annotation { "Feature Type Name" : "Feature", "Feature Type Description" : "" }
export const myFeature = defineFeature(function(context is Context, id is Id, definition is map)
    precondition{}
    {
        {
            var Q0;
            Q0=qCreatedBy(makeId("Top.planeOp"),FACE);
            var sketch = newSketch(context, id + "F0", { "sketchPlane" : qUnion([Q0])});
            skLineSegment(sketch, "E0.bottom", {"start": v(88.9, 50.8) * mm, "end": v(-88.9, 50.8) * mm});
            skLineSegment(sketch, "E0.top", {"start": v(88.9, -50.8) * mm, "end": v(-88.9, -50.8) * mm});
            skLineSegment(sketch, "E0.left", {"start": v(88.9, 50.8) * mm, "end": v(88.9, -50.8) * mm});
            skLineSegment(sketch, "E0.right", {"start": v(-88.9, 50.8) * mm, "end": v(-88.9, -50.8) * mm});
            skPoint(sketch, "E0.middle", {"position": v(0, 0) * mm});
            skText(sketch, "E1", { "text": "Brandon Ortega", "fontName": "OpenSans-Regular.ttf"});
            skLineSegment(sketch, "E2.bottom", {"start": v(95.25, 57.15) * mm, "end": v(-95.25, 57.15) * mm});
            skLineSegment(sketch, "E2.top", {"start": v(95.25, -57.15) * mm, "end": v(-95.25, -57.15) * mm});
            skLineSegment(sketch, "E2.left", {"start": v(95.25, 57.15) * mm, "end": v(95.25, -57.15) * mm});
            skLineSegment(sketch, "E2.right", {"start": v(-95.25, 57.15) * mm, "end": v(-95.25, -57.15) * mm});
            skLineSegment(sketch, "E3", {"start": v(-82.55, -15.2) * mm, "end": v(58.84, -15.2) * mm});
            skLineSegment(sketch, "E4", {"start": v(-82.55, -15.2) * mm, "end": v(-74.57, -13.6) * mm});
            skLineSegment(sketch, "E5", {"start": v(-74.57, -13.6) * mm, "end": v(-74.57, -11.23) * mm});
            skLineSegment(sketch, "E6", {"start": v(-74.57, -11.23) * mm, "end": v(-44.1, -11.23) * mm});
            skLineSegment(sketch, "E7", {"start": v(-44.1, -11.23) * mm, "end": v(-44.1, -10.52) * mm});
            skLineSegment(sketch, "E8", {"start": v(-44.1, -10.52) * mm, "end": v(-39.37, -8.24) * mm});
            skLineSegment(sketch, "E9", {"start": v(-39.37, -8.24) * mm, "end": v(-35.5, -8.24) * mm});
            skLineSegment(sketch, "E10", {"start": v(-35.5, -8.24) * mm, "end": v(-35.5, -5.61) * mm});
            skLineSegment(sketch, "E11", {"start": v(-35.5, -5.61) * mm, "end": v(-32.66, -5.61) * mm});
            skLineSegment(sketch, "E12", {"start": v(-32.66, -5.61) * mm, "end": v(-21.7, -9) * mm});
            skFitSpline(sketch, "E13", {"points": [v(-21.7, -9) * mm, v(-19.63, -9.48) * mm, v(-17.36, -9.15) * mm], "startDerivative": vector(4.23, -1.18) * mm, "endDerivative": vector(5.03, -0.02) * mm});
            skLineSegment(sketch, "E14", {"start": v(-17.36, -9.15) * mm, "end": v(11.51, -9.15) * mm});
            skLineSegment(sketch, "E15", {"start": v(11.51, -9.15) * mm, "end": v(12.43, -9.9) * mm});
            skLineSegment(sketch, "E16", {"start": v(12.43, -9.9) * mm, "end": v(12.43, -10.89) * mm});
            skLineSegment(sketch, "E17", {"start": v(12.43, -10.89) * mm, "end": v(53.63, -10.89) * mm});
            skLineSegment(sketch, "E18", {"start": v(53.63, -10.89) * mm, "end": v(54.2, -11.57) * mm});
            skLineSegment(sketch, "E19", {"start": v(54.2, -11.57) * mm, "end": v(54.2, -13.42) * mm});
            skLineSegment(sketch, "E20", {"start": v(54.2, -13.42) * mm, "end": v(58.84, -13.42) * mm});
            skLineSegment(sketch, "E21", {"start": v(58.84, -13.42) * mm, "end": v(58.84, -15.2) * mm});
            skLineSegment(sketch, "E22.MirrorCS", {"start": v(58.84, -17) * mm, "end": v(58.84, -15.2) * mm});
            skLineSegment(sketch, "E23.MirrorCS", {"start": v(54.2, -17) * mm, "end": v(58.84, -17) * mm});
            skLineSegment(sketch, "E24.MirrorCS", {"start": v(54.2, -18.85) * mm, "end": v(54.2, -17) * mm});
            skLineSegment(sketch, "E25.MirrorCS", {"start": v(53.63, -19.53) * mm, "end": v(54.2, -18.85) * mm});
            skLineSegment(sketch, "E26.MirrorCS", {"start": v(12.43, -19.53) * mm, "end": v(53.63, -19.53) * mm});
            skLineSegment(sketch, "E27.MirrorCS", {"start": v(12.43, -20.52) * mm, "end": v(12.43, -19.53) * mm});
            skLineSegment(sketch, "E28.MirrorCS", {"start": v(11.51, -21.27) * mm, "end": v(12.43, -20.52) * mm});
            skLineSegment(sketch, "E29.MirrorCS", {"start": v(-17.36, -21.27) * mm, "end": v(11.51, -21.27) * mm});
            skFitSpline(sketch, "E30.MirrorCS", {"points": [v(-21.7, -21.41) * mm, v(-19.63, -20.94) * mm, v(-17.36, -21.27) * mm], "startDerivative": vector(4.23, 1.18) * mm, "endDerivative": vector(5.03, 0.02) * mm});
            skLineSegment(sketch, "E31.MirrorCS", {"start": v(-32.66, -24.8) * mm, "end": v(-21.7, -21.41) * mm});
            skLineSegment(sketch, "E32.MirrorCS", {"start": v(-35.5, -24.8) * mm, "end": v(-32.66, -24.8) * mm});
            skLineSegment(sketch, "E33.MirrorCS", {"start": v(-35.5, -22.18) * mm, "end": v(-35.5, -24.8) * mm});
            skLineSegment(sketch, "E34.MirrorCS", {"start": v(-39.37, -22.18) * mm, "end": v(-35.5, -22.18) * mm});
            skLineSegment(sketch, "E35.MirrorCS", {"start": v(-44.1, -19.9) * mm, "end": v(-39.37, -22.18) * mm});
            skLineSegment(sketch, "E36.MirrorCS", {"start": v(-44.1, -19.2) * mm, "end": v(-44.1, -19.9) * mm});
            skLineSegment(sketch, "E37.MirrorCS", {"start": v(-74.57, -19.2) * mm, "end": v(-44.1, -19.2) * mm});
            skLineSegment(sketch, "E38.MirrorCS", {"start": v(-74.57, -16.82) * mm, "end": v(-74.57, -19.2) * mm});
            skLineSegment(sketch, "E39.MirrorCS", {"start": v(-82.55, -15.2) * mm, "end": v(-74.57, -16.82) * mm});
            skLineSegment(sketch, "E40", {"start": v(58.84, -13.42) * mm, "end": v(61.69, -13.42) * mm});
            skLineSegment(sketch, "E41", {"start": v(58.84, -17) * mm, "end": v(61.69, -17) * mm});
            skLineSegment(sketch, "E42", {"start": v(61.69, -13.42) * mm, "end": v(61.69, -17) * mm});
            skLineSegment(sketch, "E43", {"start": v(58.84, -15.2) * mm, "end": v(61.69, -15.2) * mm});
            skLineSegment(sketch, "E44", {"start": v(-19.8, -9.15) * mm, "end": v(-19.8, -4.07) * mm});
            skLineSegment(sketch, "E45", {"start": v(-19.8, -4.07) * mm, "end": v(-26.99, 3.12) * mm});
            skLineSegment(sketch, "E46", {"start": v(-16.63, -9.15) * mm, "end": v(-16.63, -3.81) * mm});
            skLineSegment(sketch, "E47", {"start": v(-14.09, -9.15) * mm, "end": v(-14.09, -3.3) * mm});
            skLineSegment(sketch, "E48", {"start": v(-14.09, -3.3) * mm, "end": v(-23.07, 5.68) * mm});
            skLineSegment(sketch, "E49", {"start": v(-10.91, -9.15) * mm, "end": v(-10.91, -3.05) * mm});
            skLineSegment(sketch, "E50", {"start": v(-8.37, -9.15) * mm, "end": v(-8.37, -2.8) * mm});
            skLineSegment(sketch, "E51", {"start": v(-8.37, -2.8) * mm, "end": v(-19.15, 7.98) * mm});
            skLineSegment(sketch, "E52", {"start": v(-5.2, -9.15) * mm, "end": v(-5.2, -2.54) * mm});
            skLineSegment(sketch, "E53", {"start": v(-24.73, 5.35) * mm, "end": v(-16.63, -3.81) * mm});
            skLineSegment(sketch, "E54", {"start": v(-20.82, 7.92) * mm, "end": v(-10.91, -3.05) * mm});
            skLineSegment(sketch, "E55", {"start": v(-16.9, 10.22) * mm, "end": v(-5.2, -2.54) * mm});
            skLineSegment(sketch, "E56.MirrorCS", {"start": v(-1.17, -21.27) * mm, "end": v(-1.17, -27.88) * mm});
            skLineSegment(sketch, "E57.MirrorCS", {"start": v(-0.4, -21.27) * mm, "end": v(-0.4, -27.62) * mm});
            skLineSegment(sketch, "E58.MirrorCS", {"start": v(0.86, -21.27) * mm, "end": v(0.86, -27.37) * mm});
            skLineSegment(sketch, "E59.MirrorCS", {"start": v(1.63, -21.27) * mm, "end": v(1.63, -27.12) * mm});
            skLineSegment(sketch, "E60.MirrorCS", {"start": v(2.9, -21.27) * mm, "end": v(2.9, -26.6) * mm});
            skLineSegment(sketch, "E61.MirrorCS", {"start": v(3.66, -21.27) * mm, "end": v(3.66, -26.35) * mm});
            skLineSegment(sketch, "E62.MirrorCS", {"start": v(3.66, -26.35) * mm, "end": v(10.84, -33.54) * mm});
            skLineSegment(sketch, "E63.MirrorCS", {"start": v(10.3, -34.08) * mm, "end": v(2.9, -26.6) * mm});
            skLineSegment(sketch, "E64.MirrorCS", {"start": v(1.63, -27.12) * mm, "end": v(10.6, -36.1) * mm});
            skLineSegment(sketch, "E65.MirrorCS", {"start": v(10.07, -36.64) * mm, "end": v(0.86, -27.37) * mm});
            skLineSegment(sketch, "E66.MirrorCS", {"start": v(-0.4, -27.62) * mm, "end": v(10.37, -38.4) * mm});
            skLineSegment(sketch, "E67.MirrorCS", {"start": v(9.83, -38.94) * mm, "end": v(-1.17, -27.88) * mm});
            skLineSegment(sketch, "E68.MirrorCS", {"start": v(2.9, -9.15) * mm, "end": v(2.9, -2.54) * mm});
            skLineSegment(sketch, "E69.MirrorCS", {"start": v(3.67, -9.15) * mm, "end": v(3.67, -2.8) * mm});
            skLineSegment(sketch, "E70.MirrorCS", {"start": v(4.94, -9.15) * mm, "end": v(4.94, -3.05) * mm});
            skLineSegment(sketch, "E71.MirrorCS", {"start": v(5.7, -9.15) * mm, "end": v(5.7, -3.3) * mm});
            skLineSegment(sketch, "E72.MirrorCS", {"start": v(6.97, -9.15) * mm, "end": v(6.97, -3.81) * mm});
            skLineSegment(sketch, "E73.MirrorCS", {"start": v(7.73, -9.15) * mm, "end": v(7.73, -4.07) * mm});
            skLineSegment(sketch, "E74.MirrorCS", {"start": v(7.73, -4.07) * mm, "end": v(14.92, 3.12) * mm});
            skLineSegment(sketch, "E75.MirrorCS", {"start": v(14.38, 3.66) * mm, "end": v(6.97, -3.81) * mm});
            skLineSegment(sketch, "E76.MirrorCS", {"start": v(5.7, -3.3) * mm, "end": v(14.68, 5.68) * mm});
            skLineSegment(sketch, "E77.MirrorCS", {"start": v(14.14, 6.22) * mm, "end": v(4.94, -3.05) * mm});
            skLineSegment(sketch, "E78.MirrorCS", {"start": v(3.67, -2.8) * mm, "end": v(14.44, 7.98) * mm});
            skLineSegment(sketch, "E79.MirrorCS", {"start": v(13.9, 8.52) * mm, "end": v(2.9, -2.54) * mm});
            skLineSegment(sketch, "E80.MirrorCS", {"start": v(-62.37, -19.2) * mm, "end": v(-62.37, -25.8) * mm});
            skLineSegment(sketch, "E81.MirrorCS", {"start": v(-63.13, -19.2) * mm, "end": v(-63.13, -25.54) * mm});
            skLineSegment(sketch, "E82.MirrorCS", {"start": v(-64.4, -19.2) * mm, "end": v(-64.4, -25.29) * mm});
            skLineSegment(sketch, "E83.MirrorCS", {"start": v(-65.16, -19.2) * mm, "end": v(-65.16, -25.04) * mm});
            skLineSegment(sketch, "E84.MirrorCS", {"start": v(-66.43, -19.2) * mm, "end": v(-66.43, -24.53) * mm});
            skLineSegment(sketch, "E85.MirrorCS", {"start": v(-67.2, -19.2) * mm, "end": v(-67.2, -24.27) * mm});
            skLineSegment(sketch, "E86.MirrorCS", {"start": v(-67.2, -24.27) * mm, "end": v(-74.38, -31.46) * mm});
            skLineSegment(sketch, "E87.MirrorCS", {"start": v(-73.84, -32) * mm, "end": v(-66.43, -24.53) * mm});
            skLineSegment(sketch, "E88.MirrorCS", {"start": v(-65.16, -25.04) * mm, "end": v(-74.14, -34.02) * mm});
            skLineSegment(sketch, "E89.MirrorCS", {"start": v(-73.6, -34.55) * mm, "end": v(-64.4, -25.29) * mm});
            skLineSegment(sketch, "E90.MirrorCS", {"start": v(-63.13, -25.54) * mm, "end": v(-73.9, -36.32) * mm});
            skLineSegment(sketch, "E91.MirrorCS", {"start": v(-73.36, -36.86) * mm, "end": v(-62.37, -25.8) * mm});
            skLineSegment(sketch, "E92", {"start": v(13.9, 8.52) * mm, "end": v(17.15, 9.7) * mm});
            skLineSegment(sketch, "E93", {"start": v(14.44, 7.98) * mm, "end": v(17.41, 8.98) * mm});
            skLineSegment(sketch, "E94", {"start": v(14.14, 6.22) * mm, "end": v(17.39, 7.4) * mm});
            skLineSegment(sketch, "E95", {"start": v(14.68, 5.68) * mm, "end": v(17.63, 6.67) * mm});
            skLineSegment(sketch, "E96", {"start": v(14.38, 3.66) * mm, "end": v(16.33, 4.18) * mm});
            skLineSegment(sketch, "E97", {"start": v(16.33, 4.18) * mm, "end": v(16.52, 3.44) * mm});
            skLineSegment(sketch, "E98", {"start": v(14.92, 3.12) * mm, "end": v(15.79, 3.25) * mm});
            skLineSegment(sketch, "E99", {"start": v(15.79, 3.25) * mm, "end": v(16.33, 1.76) * mm});
            skLineSegment(sketch, "E100", {"start": v(16.33, 1.76) * mm, "end": v(17.04, 2.02) * mm});
            skLineSegment(sketch, "E101", {"start": v(16.52, 3.44) * mm, "end": v(17.04, 2.02) * mm});
            skLineSegment(sketch, "E102", {"start": v(19.34, 7.95) * mm, "end": v(19.54, 7.21) * mm});
            skLineSegment(sketch, "E103", {"start": v(18.8, 7.01) * mm, "end": v(19.34, 5.53) * mm});
            skLineSegment(sketch, "E104", {"start": v(19.34, 5.53) * mm, "end": v(20.06, 5.79) * mm});
            skLineSegment(sketch, "E105", {"start": v(19.54, 7.21) * mm, "end": v(20.06, 5.79) * mm});
            skLineSegment(sketch, "E106", {"start": v(20.06, 10.3) * mm, "end": v(20.26, 9.57) * mm});
            skLineSegment(sketch, "E107", {"start": v(19.52, 9.37) * mm, "end": v(20.06, 7.88) * mm});
            skLineSegment(sketch, "E108", {"start": v(20.06, 7.88) * mm, "end": v(20.78, 8.14) * mm});
            skLineSegment(sketch, "E109", {"start": v(20.26, 9.57) * mm, "end": v(20.78, 8.14) * mm});
            skLineSegment(sketch, "E110", {"start": v(17.15, 9.7) * mm, "end": v(20.06, 10.3) * mm});
            skLineSegment(sketch, "E111", {"start": v(17.63, 6.67) * mm, "end": v(18.8, 7.01) * mm});
            skLineSegment(sketch, "E112", {"start": v(17.39, 7.4) * mm, "end": v(19.34, 7.95) * mm});
            skLineSegment(sketch, "E113", {"start": v(17.41, 8.98) * mm, "end": v(19.52, 9.37) * mm});
            skCircle(sketch, "E114", {"center": v(16.69, 1.89) * mm, "radius": 0.76 * mm});
            skCircle(sketch, "E115", {"center": v(19.7, 5.66) * mm, "radius": 0.76 * mm});
            skCircle(sketch, "E116", {"center": v(20.42, 8.01) * mm, "radius": 0.76 * mm});
            skLineSegment(sketch, "E117", {"start": v(-26.99, 3.12) * mm, "end": v(-24.73, 5.35) * mm});
            skLineSegment(sketch, "E118", {"start": v(-23.07, 5.68) * mm, "end": v(-20.82, 7.92) * mm});
            skLineSegment(sketch, "E119", {"start": v(-19.15, 7.98) * mm, "end": v(-16.9, 10.22) * mm});
            skCircle(sketch, "E120", {"center": v(-25.86, 4.24) * mm, "radius": 1.9 * mm});
            skCircle(sketch, "E121", {"center": v(-21.95, 6.8) * mm, "radius": 1.9 * mm});
            skCircle(sketch, "E122", {"center": v(-18.02, 9.1) * mm, "radius": 1.9 * mm});
            const initialGuessF0  = {"E1": [-0.08255, 0.0127, 1, 0, 0.01584]};
            skSetInitialGuess(sketch, initialGuessF0);
            skSolve(sketch);
        }
        {
            var Q0;
            Q0=makeQuery(id+"F0.imprint","IMPRINT",FACE,{"disambiguationData":[TD([[makeQuery(id+"F0.imprint","IMPRINT",EDGE,{"derivedFrom":sQuery(id+"F0.wireOp",EDGE,"E3")}),1.0]])]});
            var Q1;
            Q1=sQuery(id+"F0.wireOp",EDGE,"E3");
            revolve(context, id + "F1", {"entities" : qUnion([Q0]), "axis" : qUnion([Q1]), "revolveType" : RevolveType.ONE_DIRECTION, "angle" : 180 * degree});
        }
        {
            var Q0;
            Q0=makeQuery(id+"F0.imprint","IMPRINT",FACE,{"disambiguationData":[TD([[makeQuery(id+"F0.imprint","IMPRINT",EDGE,{"derivedFrom":sQuery(id+"F0.wireOp",EDGE,"E21")}),1.0]])]});
            var Q1;
            Q1=sQuery(id+"F0.wireOp",EDGE,"E43");
            revolve(context, id + "F2", {"operationType" : NewBodyOperationType.ADD, "entities" : qUnion([Q0]), "axis" : qUnion([Q1]), "revolveType" : RevolveType.ONE_DIRECTION, "angle" : 180 * degree});
        }
        {
            var Q0;
            Q0=makeQuery(id+"F0.imprint","IMPRINT",FACE,{"disambiguationData":[TD([[makeQuery(id+"F0.imprint","IMPRINT",EDGE,{"derivedFrom":sQuery(id+"F0.wireOp",EDGE,"E0.bottom")}),1.0]])]});
            var Q1;
            Q1=makeQuery(id+"F0.imprint","IMPRINT",FACE,{"disambiguationData":[TD([[makeQuery(id+"F0.imprint","IMPRINT",EDGE,{"derivedFrom":sQuery(id+"F0.wireOp",EDGE,"E0.bottom")}),-1.0]])]});
            var Q2;
            Q2=makeQuery(id+"F0.imprint","IMPRINT",FACE,{"disambiguationData":[TD([[makeQuery(id+"F0.imprint","IMPRINT",EDGE,{"derivedFrom":sQuery(id+"F0.wireOp",EDGE,"E1.sketch_text.stroke-18")}),1.0]])]});
            var Q3;
            Q3=makeQuery(id+"F0.imprint","IMPRINT",FACE,{"disambiguationData":[TD([[makeQuery(id+"F0.imprint","IMPRINT",EDGE,{"derivedFrom":sQuery(id+"F0.wireOp",EDGE,"E1.sketch_text.stroke-11")}),1.0]])]});
            var Q4;
            Q4=makeQuery(id+"F0.imprint","IMPRINT",FACE,{"disambiguationData":[TD([[makeQuery(id+"F0.imprint","IMPRINT",EDGE,{"derivedFrom":sQuery(id+"F0.wireOp",EDGE,"E1.sketch_text.stroke-57")}),1.0]])]});
            var Q5;
            Q5=makeQuery(id+"F0.imprint","IMPRINT",FACE,{"disambiguationData":[TD([[makeQuery(id+"F0.imprint","IMPRINT",EDGE,{"derivedFrom":sQuery(id+"F0.wireOp",EDGE,"E1.sketch_text.stroke-97")}),1.0]])]});
            var Q6;
            Q6=makeQuery(id+"F0.imprint","IMPRINT",FACE,{"disambiguationData":[TD([[makeQuery(id+"F0.imprint","IMPRINT",EDGE,{"derivedFrom":sQuery(id+"F0.wireOp",EDGE,"E1.sketch_text.stroke-115")}),1.0]])]});
            var Q7;
            Q7=makeQuery(id+"F0.imprint","IMPRINT",FACE,{"disambiguationData":[TD([[makeQuery(id+"F0.imprint","IMPRINT",EDGE,{"derivedFrom":sQuery(id+"F0.wireOp",EDGE,"E1.sketch_text.stroke-148")}),1.0]])]});
            var Q8;
            Q8=makeQuery(id+"F0.imprint","IMPRINT",FACE,{"disambiguationData":[TD([[makeQuery(id+"F0.imprint","IMPRINT",EDGE,{"derivedFrom":sQuery(id+"F0.wireOp",EDGE,"E1.sketch_text.stroke-202")}),1.0]])]});
            var Q9;
            Q9=makeQuery(id+"F0.imprint","IMPRINT",FACE,{"disambiguationData":[TD([[makeQuery(id+"F0.imprint","IMPRINT",EDGE,{"derivedFrom":sQuery(id+"F0.wireOp",EDGE,"E1.sketch_text.stroke-245")}),1.0]])]});
            var Q10;
            Q10=makeQuery(id+"F0.imprint","IMPRINT",FACE,{"disambiguationData":[TD([[makeQuery(id+"F0.imprint","IMPRINT",EDGE,{"derivedFrom":sQuery(id+"F0.wireOp",EDGE,"E1.sketch_text.stroke-236")}),1.0]])]});
            var Q11;
            Q11=makeQuery(id+"F0.imprint","IMPRINT",FACE,{"disambiguationData":[TD([[makeQuery(id+"F0.imprint","IMPRINT",EDGE,{"derivedFrom":sQuery(id+"F0.wireOp",EDGE,"E1.sketch_text.stroke-270")}),1.0]])]});
            var Q12;
            Q12=makeQuery(id+"F0.imprint","IMPRINT",FACE,{"disambiguationData":[TD([[makeQuery(id+"F0.imprint","IMPRINT",EDGE,{"derivedFrom":sQuery(id+"F0.wireOp",EDGE,"E1.sketch_text.stroke-0")}),-1.0]])]});
            var Q13;
            Q13=makeQuery(id+"F0.imprint","IMPRINT",FACE,{"disambiguationData":[TD([[makeQuery(id+"F0.imprint","IMPRINT",EDGE,{"derivedFrom":sQuery(id+"F0.wireOp",EDGE,"E1.sketch_text.stroke-25")}),-1.0]])]});
            var Q14;
            Q14=makeQuery(id+"F0.imprint","IMPRINT",FACE,{"disambiguationData":[TD([[makeQuery(id+"F0.imprint","IMPRINT",EDGE,{"derivedFrom":sQuery(id+"F0.wireOp",EDGE,"E1.sketch_text.stroke-38")}),-1.0]])]});
            var Q15;
            Q15=makeQuery(id+"F0.imprint","IMPRINT",FACE,{"disambiguationData":[TD([[makeQuery(id+"F0.imprint","IMPRINT",EDGE,{"derivedFrom":sQuery(id+"F0.wireOp",EDGE,"E1.sketch_text.stroke-65")}),-1.0]])]});
            var Q16;
            Q16=makeQuery(id+"F0.imprint","IMPRINT",FACE,{"disambiguationData":[TD([[makeQuery(id+"F0.imprint","IMPRINT",EDGE,{"derivedFrom":sQuery(id+"F0.wireOp",EDGE,"E1.sketch_text.stroke-82")}),-1.0]])]});
            var Q17;
            Q17=makeQuery(id+"F0.imprint","IMPRINT",FACE,{"disambiguationData":[TD([[makeQuery(id+"F0.imprint","IMPRINT",EDGE,{"derivedFrom":sQuery(id+"F0.wireOp",EDGE,"E1.sketch_text.stroke-106")}),-1.0]])]});
            var Q18;
            Q18=makeQuery(id+"F0.imprint","IMPRINT",FACE,{"disambiguationData":[TD([[makeQuery(id+"F0.imprint","IMPRINT",EDGE,{"derivedFrom":sQuery(id+"F0.wireOp",EDGE,"E1.sketch_text.stroke-123")}),-1.0]])]});
            var Q19;
            Q19=makeQuery(id+"F0.imprint","IMPRINT",FACE,{"disambiguationData":[TD([[makeQuery(id+"F0.imprint","IMPRINT",EDGE,{"derivedFrom":sQuery(id+"F0.wireOp",EDGE,"E1.sketch_text.stroke-140")}),-1.0]])]});
            var Q20;
            Q20=makeQuery(id+"F0.imprint","IMPRINT",FACE,{"disambiguationData":[TD([[makeQuery(id+"F0.imprint","IMPRINT",EDGE,{"derivedFrom":sQuery(id+"F0.wireOp",EDGE,"E1.sketch_text.stroke-156")}),-1.0]])]});
            var Q21;
            Q21=makeQuery(id+"F0.imprint","IMPRINT",FACE,{"disambiguationData":[TD([[makeQuery(id+"F0.imprint","IMPRINT",EDGE,{"derivedFrom":sQuery(id+"F0.wireOp",EDGE,"E1.sketch_text.stroke-169")}),-1.0]])]});
            var Q22;
            Q22=makeQuery(id+"F0.imprint","IMPRINT",FACE,{"disambiguationData":[TD([[makeQuery(id+"F0.imprint","IMPRINT",EDGE,{"derivedFrom":sQuery(id+"F0.wireOp",EDGE,"E1.sketch_text.stroke-188")}),-1.0]])]});
            var Q23;
            Q23=makeQuery(id+"F0.imprint","IMPRINT",FACE,{"disambiguationData":[TD([[makeQuery(id+"F0.imprint","IMPRINT",EDGE,{"derivedFrom":sQuery(id+"F0.wireOp",EDGE,"E1.sketch_text.stroke-207")}),-1.0]])]});
            var Q24;
            Q24=makeQuery(id+"F0.imprint","IMPRINT",FACE,{"disambiguationData":[TD([[makeQuery(id+"F0.imprint","IMPRINT",EDGE,{"derivedFrom":sQuery(id+"F0.wireOp",EDGE,"E1.sketch_text.stroke-251")}),-1.0]])]});
            extrude(context, id + "F3", {"entities" : qUnion([Q0, Q1, Q2, Q3, Q4, Q5, Q6, Q7, Q8, Q9, Q10, Q11, Q12, Q13, Q14, Q15, Q16, Q17, Q18, Q19, Q20, Q21, Q22, Q23, Q24]), "oppositeDirection" : true, "depth" : 2.54 * mm, "offsetDistance" : 25.4 * mm});
        }
        {
            var Q0;
            Q0=makeQuery(id+"F0.imprint","IMPRINT",FACE,{"disambiguationData":[TD([[makeQuery(id+"F0.imprint","IMPRINT",EDGE,{"derivedFrom":sQuery(id+"F0.wireOp",EDGE,"E0.bottom")}),-1.0]])]});
            extrude(context, id + "F4", {"entities" : qUnion([Q0]), "operationType" : NewBodyOperationType.ADD, "depth" : 12.7 * mm, "offsetDistance" : 25.4 * mm});
        }
        {
            var Q0;
            Q0=makeQuery(id+"F0.imprint","IMPRINT",FACE,{"disambiguationData":[TD([[makeQuery(id+"F0.imprint","IMPRINT",EDGE,{"derivedFrom":sQuery(id+"F0.wireOp",EDGE,"E1.sketch_text.stroke-0")}),-1.0]])]});
            var Q1;
            Q1=makeQuery(id+"F0.imprint","IMPRINT",FACE,{"disambiguationData":[TD([[makeQuery(id+"F0.imprint","IMPRINT",EDGE,{"derivedFrom":sQuery(id+"F0.wireOp",EDGE,"E1.sketch_text.stroke-25")}),-1.0]])]});
            var Q2;
            Q2=makeQuery(id+"F0.imprint","IMPRINT",FACE,{"disambiguationData":[TD([[makeQuery(id+"F0.imprint","IMPRINT",EDGE,{"derivedFrom":sQuery(id+"F0.wireOp",EDGE,"E1.sketch_text.stroke-38")}),-1.0]])]});
            var Q3;
            Q3=makeQuery(id+"F0.imprint","IMPRINT",FACE,{"disambiguationData":[TD([[makeQuery(id+"F0.imprint","IMPRINT",EDGE,{"derivedFrom":sQuery(id+"F0.wireOp",EDGE,"E1.sketch_text.stroke-65")}),-1.0]])]});
            var Q4;
            Q4=makeQuery(id+"F0.imprint","IMPRINT",FACE,{"disambiguationData":[TD([[makeQuery(id+"F0.imprint","IMPRINT",EDGE,{"derivedFrom":sQuery(id+"F0.wireOp",EDGE,"E1.sketch_text.stroke-82")}),-1.0]])]});
            var Q5;
            Q5=makeQuery(id+"F0.imprint","IMPRINT",FACE,{"disambiguationData":[TD([[makeQuery(id+"F0.imprint","IMPRINT",EDGE,{"derivedFrom":sQuery(id+"F0.wireOp",EDGE,"E1.sketch_text.stroke-106")}),-1.0]])]});
            var Q6;
            Q6=makeQuery(id+"F0.imprint","IMPRINT",FACE,{"disambiguationData":[TD([[makeQuery(id+"F0.imprint","IMPRINT",EDGE,{"derivedFrom":sQuery(id+"F0.wireOp",EDGE,"E1.sketch_text.stroke-140")}),-1.0]])]});
            var Q7;
            Q7=makeQuery(id+"F0.imprint","IMPRINT",FACE,{"disambiguationData":[TD([[makeQuery(id+"F0.imprint","IMPRINT",EDGE,{"derivedFrom":sQuery(id+"F0.wireOp",EDGE,"E1.sketch_text.stroke-123")}),-1.0]])]});
            var Q8;
            Q8=makeQuery(id+"F0.imprint","IMPRINT",FACE,{"disambiguationData":[TD([[makeQuery(id+"F0.imprint","IMPRINT",EDGE,{"derivedFrom":sQuery(id+"F0.wireOp",EDGE,"E1.sketch_text.stroke-156")}),-1.0]])]});
            var Q9;
            Q9=makeQuery(id+"F0.imprint","IMPRINT",FACE,{"disambiguationData":[TD([[makeQuery(id+"F0.imprint","IMPRINT",EDGE,{"derivedFrom":sQuery(id+"F0.wireOp",EDGE,"E1.sketch_text.stroke-169")}),-1.0]])]});
            var Q10;
            Q10=makeQuery(id+"F0.imprint","IMPRINT",FACE,{"disambiguationData":[TD([[makeQuery(id+"F0.imprint","IMPRINT",EDGE,{"derivedFrom":sQuery(id+"F0.wireOp",EDGE,"E1.sketch_text.stroke-188")}),-1.0]])]});
            var Q11;
            Q11=makeQuery(id+"F0.imprint","IMPRINT",FACE,{"disambiguationData":[TD([[makeQuery(id+"F0.imprint","IMPRINT",EDGE,{"derivedFrom":sQuery(id+"F0.wireOp",EDGE,"E1.sketch_text.stroke-207")}),-1.0]])]});
            var Q12;
            Q12=makeQuery(id+"F0.imprint","IMPRINT",FACE,{"disambiguationData":[TD([[makeQuery(id+"F0.imprint","IMPRINT",EDGE,{"derivedFrom":sQuery(id+"F0.wireOp",EDGE,"E1.sketch_text.stroke-251")}),-1.0]])]});
            extrude(context, id + "F5", {"entities" : qUnion([Q0, Q1, Q2, Q3, Q4, Q5, Q6, Q7, Q8, Q9, Q10, Q11, Q12]), "depth" : 12.7 * mm, "offsetDistance" : 25.4 * mm});
        }
    });